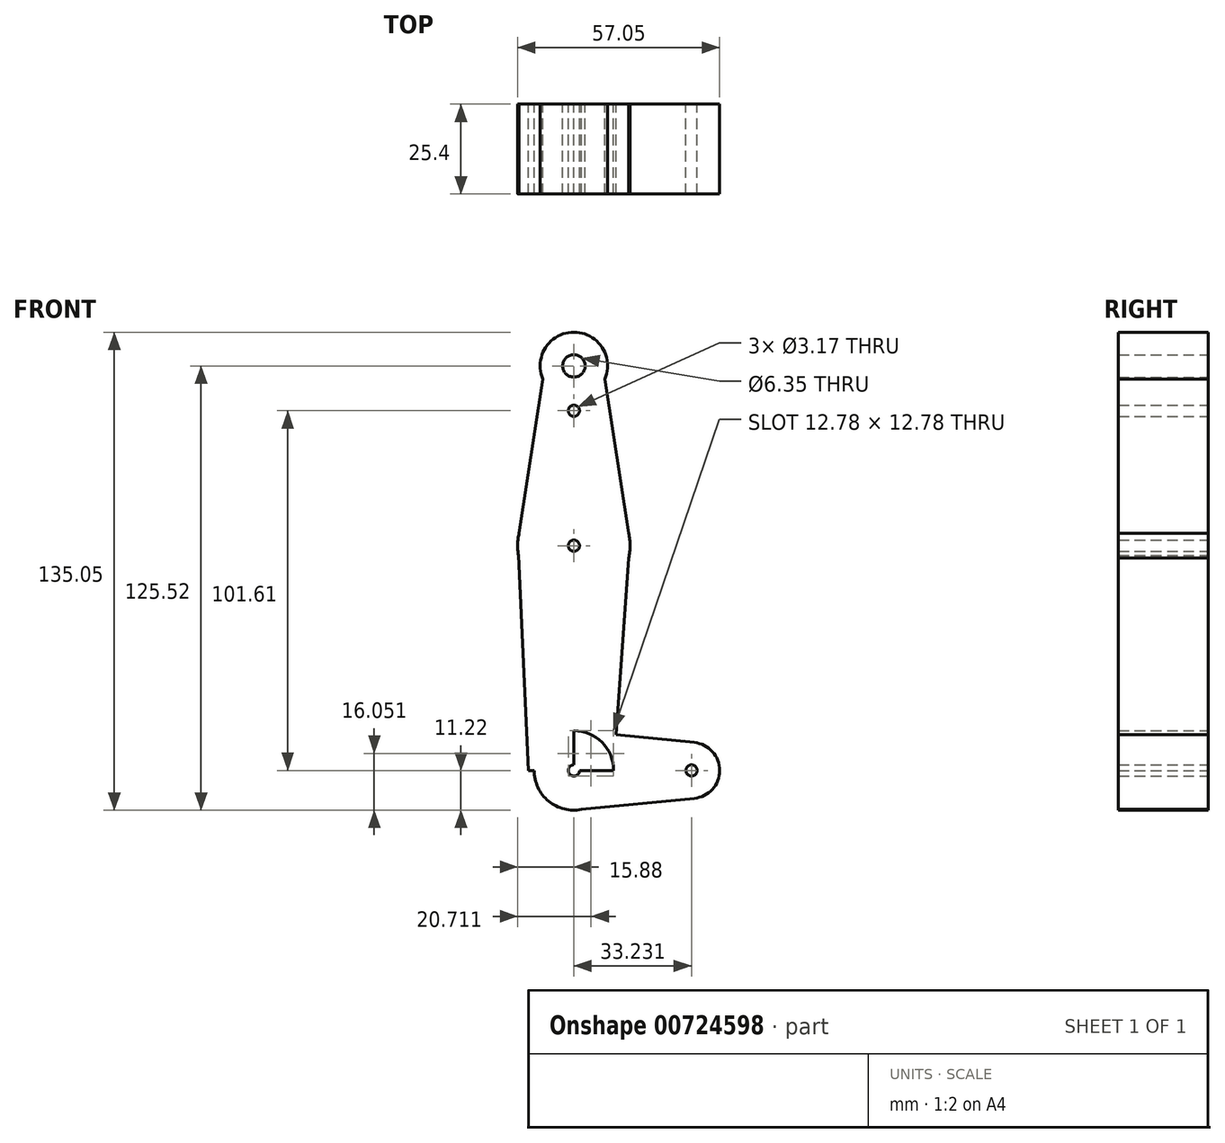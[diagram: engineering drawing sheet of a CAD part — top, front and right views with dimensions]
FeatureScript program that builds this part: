
annotation { "Feature Type Name" : "Feature", "Feature Type Description" : "" }
export const myFeature = defineFeature(function(context is Context, id is Id, definition is map)
    precondition{}
    {
        {
            var Q0;
            Q0=qCreatedBy(makeId("Front.planeOp"),FACE);
            var sketch = newSketch(context, id + "F0", { "sketchPlane" : qUnion([Q0])});
            skLineSegment(sketch, "E0", {"start": v(0, 0) * mm, "end": v(0, 114.3) * mm});
            skLineSegment(sketch, "E1", {"start": v(0, 0) * mm, "end": v(33.23, 0) * mm});
            skCircle(sketch, "E2", {"center": v(0, 114.3) * mm, "radius": 9.53 * mm});
            skCircle(sketch, "E3", {"center": v(0, 0) * mm, "radius": 11.22 * mm});
            skCircle(sketch, "E4", {"center": v(33.23, 0) * mm, "radius": 7.94 * mm});
            skCircle(sketch, "E5", {"center": v(0, 63.5) * mm, "radius": 15.88 * mm});
            skLineSegment(sketch, "E6", {"start": v(-8.76, 110.55) * mm, "end": v(-15.82, 64.8) * mm});
            skLineSegment(sketch, "E7", {"start": v(8.76, 110.55) * mm, "end": v(15.82, 64.8) * mm});
            skLineSegment(sketch, "E8", {"start": v(15.82, 64.8) * mm, "end": v(11.25, 0) * mm});
            skLineSegment(sketch, "E9", {"start": v(0, 11.22) * mm, "end": v(34, 7.9) * mm});
            skPoint(sketch, "E10.startSnap0", {"position": v(-13.53, 32.4) * mm});
            skLineSegment(sketch, "E11", {"start": v(0, -11.22) * mm, "end": v(34, -7.9) * mm});
            skLineSegment(sketch, "E12", {"start": v(11.25, 0) * mm, "end": v(-12.88, 0) * mm});
            skLineSegment(sketch, "E13", {"start": v(-15.82, 64.8) * mm, "end": v(-12.88, 0) * mm});
            skCircle(sketch, "E14", {"center": v(0, 101.6) * mm, "radius": 1.59 * mm});
            skCircle(sketch, "E15", {"center": v(0, 63.5) * mm, "radius": 1.59 * mm});
            skCircle(sketch, "E16", {"center": v(0, 114.3) * mm, "radius": 3.18 * mm});
            skCircle(sketch, "E17", {"center": v(0, 0) * mm, "radius": 1.59 * mm});
            skCircle(sketch, "E18", {"center": v(33.23, 0) * mm, "radius": 1.59 * mm});
            skSolve(sketch);
        }
        {
            var Q0;
            Q0 = qSketchRegion(id + "F0", true);
            extrude(context, id + "F1", {"entities" : qUnion([Q0]), "depth" : 25.4 * mm, "offsetDistance" : 25.4 * mm});
        }
    });
